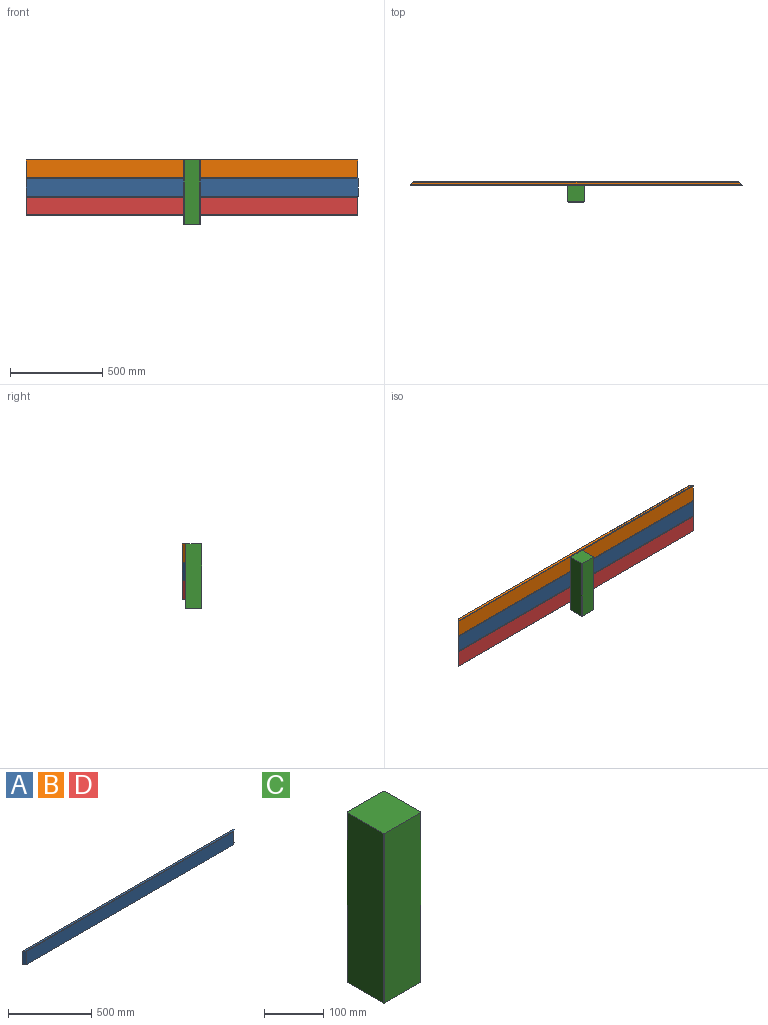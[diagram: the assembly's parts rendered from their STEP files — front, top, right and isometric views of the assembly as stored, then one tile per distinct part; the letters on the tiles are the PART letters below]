
ASSEMBLY  parts=4 mates=3
PART A: 10 faces, bbox 1800x18x100 mm
  f0: plane 1800x96mm, normal (0,1,0), area 172800mm2, adj f4,f5,f6,f7
  f1: plane 1764x96mm, normal (0,-1,0), area 169344mm2, adj f4,f5,f8,f9
  f2: plane 1796x14mm, normal (0,0,1), area 24948mm2, adj f4,f5,f7,f9
  f3: plane 1796x14mm, normal (0,0,-1), area 24948mm2, adj f4,f5,f6,f8
  f4: plane 100x18mm, normal (-0.71,-0.71,0), area 2534.3mm2, adj f0,f1,f2,f3,f6,f7,f8,f9
  f5: plane 100x18mm, normal (0.71,-0.71,0), area 2534.3mm2, adj f0,f1,f2,f3,f6,f7,f8,f9
  f6: plane 1800x2mm, normal (0,0.71,-0.71), area 5085.5mm2, adj f0,f3,f4,f5
  f7: plane 1800x2mm, normal (0,0.71,0.71), area 5085.5mm2, adj f0,f2,f4,f5
  f8: plane 1768x2mm, normal (0,-0.71,-0.71), area 4995mm2, adj f1,f3,f4,f5
  f9: plane 1768x2mm, normal (0,-0.71,0.71), area 4995mm2, adj f1,f2,f4,f5
PART B: same geometry as A
PART C: 10 faces, bbox 90x90x350 mm
  f0: plane 350x86mm, normal (0,-1,0), area 30100mm2, adj f4,f5,f6,f7
  f1: plane 350x86mm, normal (1,0,0), area 30100mm2, adj f4,f5,f6,f9
  f2: plane 350x86mm, normal (0,1,0), area 30100mm2, adj f4,f5,f8,f9
  f3: plane 350x86mm, normal (-1,0,0), area 30100mm2, adj f4,f5,f7,f8
  f4: plane 90x90mm, normal (0,0,1), area 8092mm2, adj f0,f1,f2,f3,f6,f7,f8,f9
  f5: plane 90x90mm, normal (0,0,-1), area 8092mm2, adj f0,f1,f2,f3,f6,f7,f8,f9
  f6: plane 350x2mm, normal (0.71,-0.71,0), area 989.9mm2, adj f0,f1,f4,f5
  f7: plane 350x2mm, normal (-0.71,-0.71,0), area 989.9mm2, adj f0,f3,f4,f5
  f8: plane 350x2mm, normal (-0.71,0.71,0), area 989.9mm2, adj f2,f3,f4,f5
  f9: plane 350x2mm, normal (0.71,0.71,0), area 989.9mm2, adj f1,f2,f4,f5
PART D: same geometry as A
PLACE A rot(axis=(0,0,1),180deg) t=(-586.53,68.28,-303.2)mm
PLACE B rot(axis=(1,0,0),180deg) t=(-570.23,68.28,-102.2)mm
PLACE C rot(axis=(0,-1,0),180deg) t=(-555.96,62.92,-103.2)mm
PLACE D rot(axis=(1,0,0),180deg) t=(-570.23,68.28,-304.2)mm
MATE fastened B.f0 <-> C.f2  axis (0,-1,0) through (-578.38,160.76,-152.2)mm
MATE fastened C.f2 <-> D.f0  axis (0,1,0) through (-578.38,160.76,-278.2)mm
MATE fastened A.f0 <-> C.f2  axis (0,-1,0) through (-578.38,160.76,-253.2)mm
